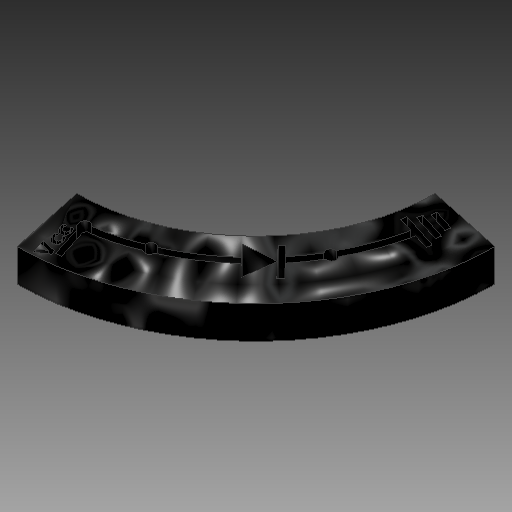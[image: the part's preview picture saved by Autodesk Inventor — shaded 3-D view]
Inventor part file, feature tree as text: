
AUTODESK INVENTOR PART (.ipt)
format: ipt  version: 2017 (Build 210142000, 142)  size: 385,536 bytes
history: native  units: in
note: dims shown in document units (in); Inventor stores cm internally (conversion verified against a paired STEP export)
features: sketch x3, extrude x2, revolve x1, projected_geometry x1
ambient origin geometry x8: Origin, YZ Plane, XZ Plane, XY Plane, X Axis, Y Axis, Z Axis, Center Point
bodies: Solid1 (feature_tree)
feature tree (7):
  revolve  "Revolution1"  [1 undecoded]
  extrude  "Extrusion1"  Depth=0.05in
  extrude  "Extrusion3"  Depth=0.025in
  sketch  "Sketch1"  dims[d0=0.8265in d1=0.175in]
  sketch  "Sketch2"  dims[d2=0.05in d3=0.1in]
  projected_geometry  "Projected Loop1"
  sketch  "Sketch4"  dims[d4=0.15in d5=0.275in d6=90.0deg d18=0.05in d26=0.05in d29=0.135in d31=0.025in d34=0.15in d35=0.05in d36=0.3in d39=0.135in d40=0.3in d42=0.025in d48=0.05in d49=0.3in d50=0.025in d52=0.3in d53=0.135in d54=0.025in d55=0.135in d56=0.05in d57=0.025in d59=0.15in d60=0.135in d61=0.1in d62=0.075in d63=0.025in d64=0.025in d65=0.025in d67=0.025in d69=0.1in d70=0.0in d74=0.0515in d75=0.0125in d77=0.0515in d78=0.025in d79=1.0in d80=0.0in]
note: 1 required parameter value undecoded (feature->parameter linkage not recoverable at this tier; creation-order binding heuristic only, values carry confidence <= 0.55)
